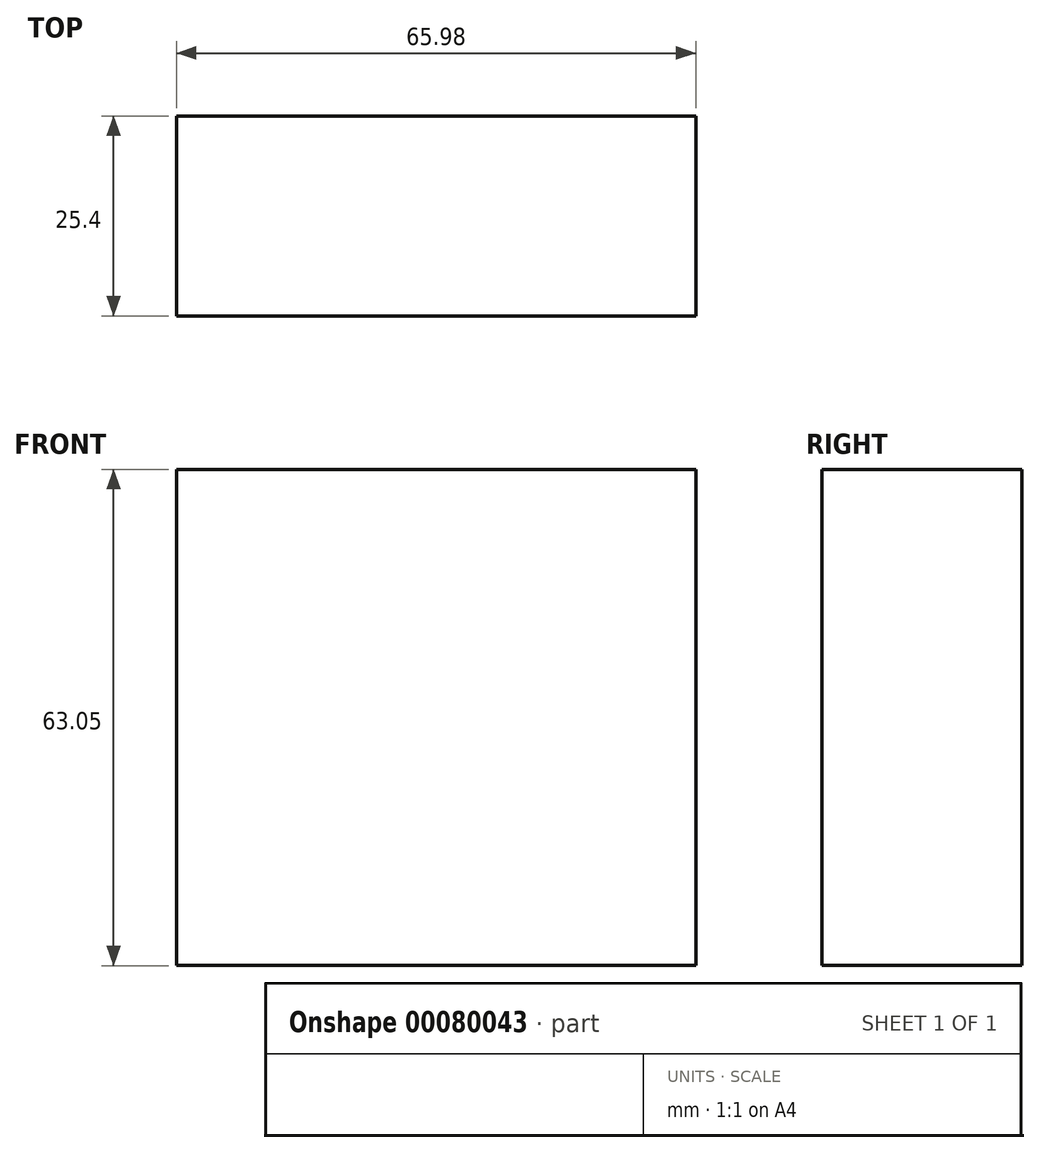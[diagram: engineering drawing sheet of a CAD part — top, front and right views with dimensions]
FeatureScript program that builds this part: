
annotation { "Feature Type Name" : "Feature", "Feature Type Description" : "" }
export const myFeature = defineFeature(function(context is Context, id is Id, definition is map)
    precondition{}
    {
        {
            var Q0;
            Q0=qCreatedBy(makeId("Front.planeOp"),FACE);
            var sketch = newSketch(context, id + "F0", { "sketchPlane" : qUnion([Q0])});
            skLineSegment(sketch, "E0.bottom", {"start": v(-29.65, 26.58) * mm, "end": v(36.33, 26.58) * mm});
            skLineSegment(sketch, "E0.top", {"start": v(-29.65, -36.47) * mm, "end": v(36.33, -36.47) * mm});
            skLineSegment(sketch, "E0.left", {"start": v(-29.65, 26.58) * mm, "end": v(-29.65, -36.47) * mm});
            skLineSegment(sketch, "E0.right", {"start": v(36.33, 26.58) * mm, "end": v(36.33, -36.47) * mm});
            skSolve(sketch);
        }
        {
            var Q0;
            Q0 = qSketchRegion(id + "F0", true);
            extrude(context, id + "F1", {"entities" : qUnion([Q0]), "depth" : 25.4 * mm});
        }
    });
